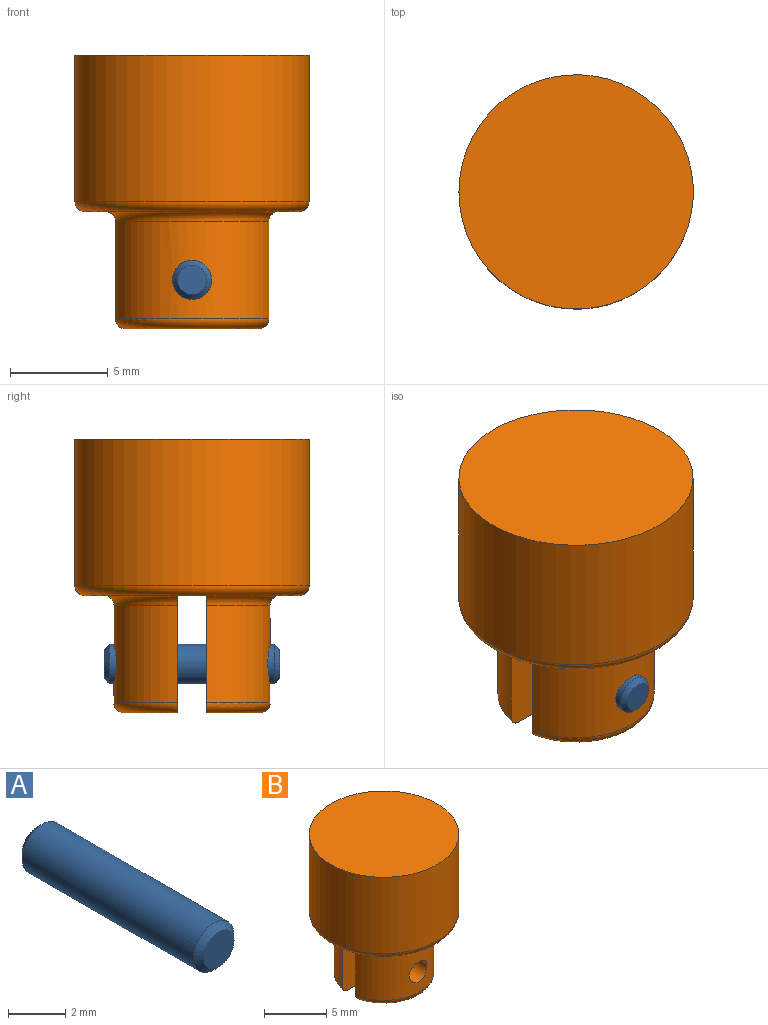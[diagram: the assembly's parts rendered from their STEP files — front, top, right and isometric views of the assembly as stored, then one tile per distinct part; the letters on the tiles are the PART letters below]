
ASSEMBLY  parts=2 mates=1
PART A: 5 faces, bbox 2x9x2 mm
  f0: cylinder r=1mm len=8.5mm, axis (0,1,0), area 53.4mm2, adj f3,f4
  f1: plane 1.5x1.5mm, normal (0,-1,0), area 1.8mm2, adj f4
  f2: plane 1.5x1.5mm, normal (0,1,0), area 1.8mm2, adj f3
  f3: cone r=1mm half-angle=45deg, axis (0,-1,0), area 1.9mm2, adj f0,f2
  f4: cone r=0.75mm half-angle=45deg, axis (0,1,0), area 1.9mm2, adj f0,f1
PART B: 16 faces, bbox 13x13x14 mm
  f0: cylinder r=4mm len=7.86mm, axis (0,0,-1), area 52.1mm2, adj f2,f3,f13,f14
  f1: plane 6.84x2.75mm, normal (0,0,-1), area 14mm2, adj f11,f12
  f2: torus R=4.5mm, axis (0,0,-1), area 9.1mm2, adj f0,f6,f13
  f3: torus R=3.5mm, axis (0,0,-1), area 8.2mm2, adj f0,f8,f13
  f4: plane 12x12mm, normal (0,0,1), area 113.1mm2, adj f5
  f5: cylinder r=6mm len=12mm, axis (0,0,-1), area 282.7mm2, adj f4,f9
  f6: plane 11x11mm, normal (0,0,-1), area 44.9mm2, adj f2,f9,f10,f12,f13
  f7: cylinder r=4mm len=7.86mm, axis (0,0,-1), area 52.1mm2, adj f10,f11,f12,f15
  f8: plane 6.84x2.75mm, normal (0,0,-1), area 14mm2, adj f3,f13
  f9: torus R=5.5mm, axis (0,0,-1), area 28.7mm2, adj f5,f6
  f10: torus R=4.5mm, axis (0,0,-1), area 9.1mm2, adj f6,f7,f12
  f11: torus R=3.5mm, axis (0,0,-1), area 8.2mm2, adj f1,f7,f12
  f12: plane 8.87x6mm, normal (0,1,0), area 44mm2, adj f1,f6,f7,f10,f11,f15
  f13: plane 8.87x6mm, normal (0,-1,0), area 44mm2, adj f0,f2,f3,f6,f8,f14
  f14: cylinder r=1mm len=3.25mm, axis (0,-1,0), area 20mm2, adj f0,f13
  f15: cylinder r=1mm len=3.25mm, axis (0,-1,0), area 20mm2, adj f7,f12
PLACE A at identity
PLACE B at identity fixed
MATE fastened A.f0 <-> B.f14  axis (0,1,0) through (0,0,-3.5)mm
